# Revit family: Plymold-Contour-Freestanding_Bench
name_source: partatom
category: Furniture
units: mm (PartAtom-declared; Revit-internal decimal feet)

## family parameters
Always vertical = Yes
Cut with Voids When Loaded = No
OmniClass Number = 23.40.20.00
OmniClass Title = General Furniture and Specialties
Render Appearance Source = Family Geometry
Room Calculation Point = No
Shared = No
Work Plane-Based = No

## types (3) — shared parameters
Assembly Code = E2020200
Cap Finish = PLY - Plastic Black
Default Elevation = 0"
Depth = 20 1/2"
Frame Finish = PLY - Onyx Black Powdercoat
Glides Finish = PLY - Plastic Black
Height = 36"
Keynote = 12500
Manufacturer = Plymold
Product Documentation Link = https://plymold.com
Revit File Built By = https://servex-us.com
Seat Finish = PLY - Wood Mahogany
Support Finish = PLY - Onyx Black Powdercoat
Sustainability = https://plymold.com
Type Comments = Contour
URL = https://plymold.com

## per-type parameters (varying)
| type | Description | Width |
| CBFR042 | Contour Freestanding Bench Un - 42"W x 20 1/2"D x 36"H | 42" |
| CBFR047 | Contour Freestanding Bench Un - 47"W x 20 1/2"D x 36"H | 47" |
| CBFR059 | Contour Freestanding Bench Un - 59"W x 20 1/2"D x 36"H | 59" |

note: column(s) folded — value = type name in every type: Model

## geometry (parser evidence)
native form markers: Sweep x9
no freeform markers — native parametric forms only
